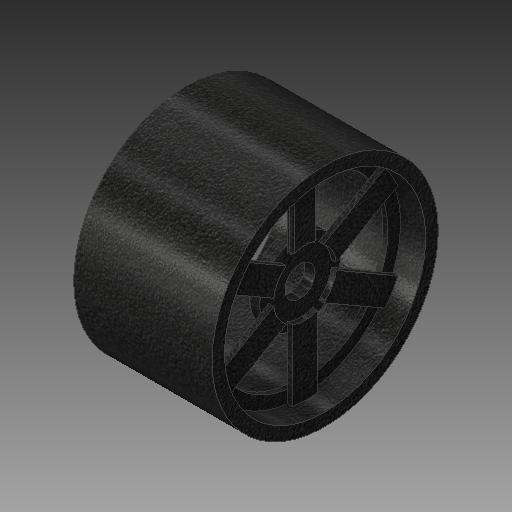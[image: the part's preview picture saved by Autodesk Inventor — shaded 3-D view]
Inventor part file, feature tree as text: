
AUTODESK INVENTOR PART (.ipt)
format: ipt  version: 2019 (Build 230136000, 136)  size: 321,536 bytes
history: native  units: mm
features: extrude x4, sketch x4, other x2, fillet x1, pattern_circular x1
ambient origin geometry x8: Origin, YZ Plane, XZ Plane, XY Plane, X Axis, Y Axis, Z Axis, Center Point
bodies: Body1 (feature_tree)
feature tree (12):
  other  "Твердое тело1"
  extrude  "Выдавливание1"  Depth=90.0mm
  other  "РабПлоскость1"
  extrude  "Выдавливание2"  Depth=5.0mm
  extrude  "Выдавливание3"  Depth=55.0mm TaperAngle=0.0deg
  extrude  "Выдавливание4"  [1 undecoded]
  fillet  "Сопряжение1"  Radius=5.0mm
  pattern_circular  "Круговой массив1"  [2 undecoded]
  sketch  "Эскиз1"
  sketch  "Эскиз2"
  sketch  "Эскиз3"
  sketch  "Эскиз4"
note: 3 required parameter values undecoded (feature->parameter linkage not recoverable at this tier; creation-order binding heuristic only, values carry confidence <= 0.55)
